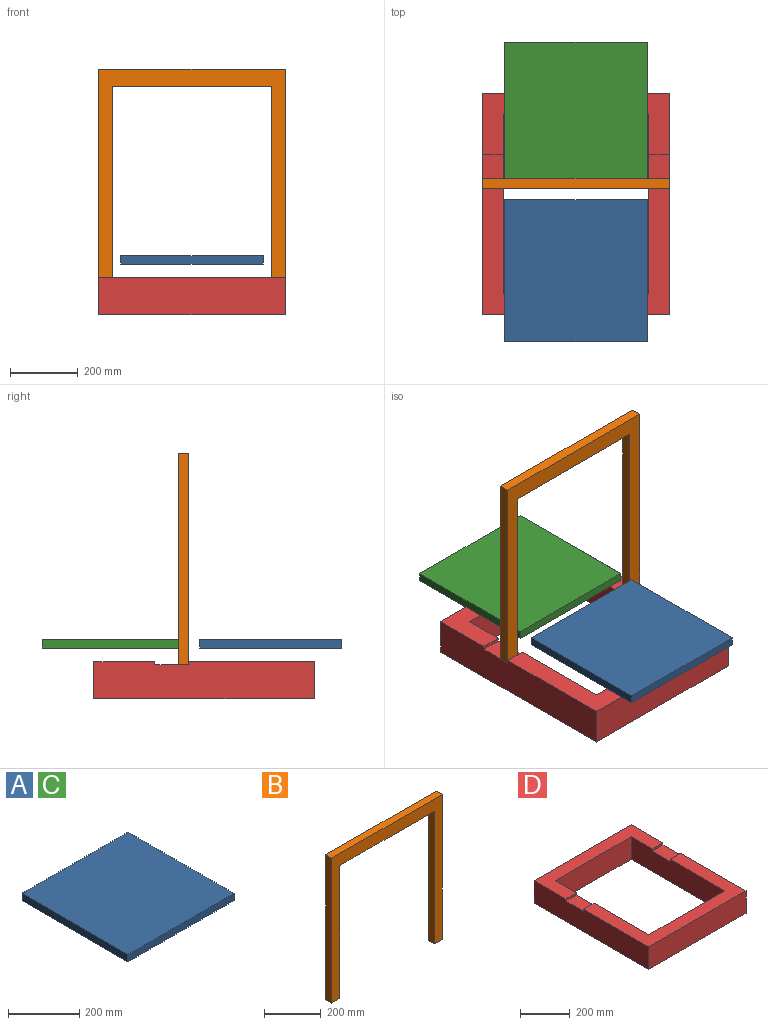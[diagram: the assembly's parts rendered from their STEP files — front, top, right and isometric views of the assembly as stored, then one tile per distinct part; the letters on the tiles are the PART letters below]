
ASSEMBLY  parts=4 mates=5
PART A: 6 faces, bbox 420x420x25 mm
  f0: plane 420x25mm, normal (1,0,0), area 10500mm2, adj f1,f3,f4,f5
  f1: plane 420x25mm, normal (0,1,0), area 10500mm2, adj f0,f2,f4,f5
  f2: plane 420x25mm, normal (-1,0,0), area 10500mm2, adj f1,f3,f4,f5
  f3: plane 420x25mm, normal (0,-1,0), area 10500mm2, adj f0,f2,f4,f5
  f4: plane 420x420mm, normal (0,0,1), area 176400mm2, adj f0,f1,f2,f3
  f5: plane 420x420mm, normal (0,0,-1), area 176400mm2, adj f0,f1,f2,f3
PART B: 10 faces, bbox 550x30x625 mm
  f0: plane 573x30mm, normal (1,0,0), area 17190mm2, adj f1,f7,f8,f9
  f1: plane 470x30mm, normal (0,0,-1), area 14100mm2, adj f0,f2,f8,f9
  f2: plane 573x30mm, normal (-1,0,0), area 17190mm2, adj f1,f3,f8,f9
  f3: plane 40x30mm, normal (0,0,-1), area 1200mm2, adj f2,f4,f8,f9
  f4: plane 625x30mm, normal (1,0,0), area 18750mm2, adj f3,f5,f8,f9
  f5: plane 550x30mm, normal (0,0,1), area 16500mm2, adj f4,f6,f8,f9
  f6: plane 625x30mm, normal (-1,0,0), area 18750mm2, adj f5,f7,f8,f9
  f7: plane 40x30mm, normal (0,0,-1), area 1200mm2, adj f0,f6,f8,f9
  f8: plane 625x550mm, normal (0,-1,0), area 74440mm2, adj f0,f1,f2,f3,f4,f5,f6,f7
  f9: plane 625x550mm, normal (0,1,0), area 74440mm2, adj f0,f1,f2,f3,f4,f5,f6,f7
PART C: same geometry as A
PART D: 17 faces, bbox 550x650x110 mm
  f0: plane 530x110mm, normal (1,0,0), area 57300mm2, adj f3,f7,f8,f9,f10,f11,f12,f13
  f1: plane 530x110mm, normal (-1,0,0), area 57300mm2, adj f3,f7,f8,f9,f10,f14,f15,f16
  f2: plane 650x110mm, normal (-1,0,0), area 70500mm2, adj f3,f4,f6,f9,f10,f11,f12,f13
  f3: plane 550x180mm, normal (0,0,1), area 47400mm2, adj f0,f1,f2,f5,f6,f8,f13,f14
  f4: plane 550x110mm, normal (0,-1,0), area 60500mm2, adj f2,f5,f9,f10
  f5: plane 650x110mm, normal (1,0,0), area 70500mm2, adj f3,f4,f6,f9,f10,f14,f15,f16
  f6: plane 550x110mm, normal (0,1,0), area 60500mm2, adj f2,f3,f5,f10
  f7: plane 430x110mm, normal (0,1,0), area 47300mm2, adj f0,f1,f9,f10
  f8: plane 430x110mm, normal (0,-1,0), area 47300mm2, adj f0,f1,f3,f10
  f9: plane 550x370mm, normal (0,0,1), area 70200mm2, adj f0,f1,f2,f4,f5,f7,f12,f15
  f10: plane 650x550mm, normal (0,0,-1), area 129600mm2, adj f0,f1,f2,f4,f5,f6,f7,f8
  f11: plane 100x60mm, normal (0,0,1), area 6000mm2, adj f0,f2,f12,f13
  f12: plane 60x10mm, normal (0,1,0), area 600mm2, adj f0,f2,f9,f11
  f13: plane 60x10mm, normal (0,-1,0), area 600mm2, adj f0,f2,f3,f11
  f14: plane 60x10mm, normal (0,-1,0), area 600mm2, adj f1,f3,f5,f16
  f15: plane 60x10mm, normal (0,1,0), area 600mm2, adj f1,f5,f9,f16
  f16: plane 100x60mm, normal (0,0,1), area 6000mm2, adj f1,f5,f14,f15
PLACE A rot(axis=(0,0,1),0deg) t=(275,128.03,150)mm
PLACE B t=(0,400,100)mm
PLACE C t=(275,592.66,150)mm
PLACE D at identity
MATE planar B.f6 <-> D.f2  axis (-1,0,0) through (0,385,412.5)mm
MATE planar B.f8 <-> D.f12  axis (0,-1,0) through (275,370,506.56)mm
MATE parallel D.f9 <-> A.f5  axis (0,0,1) through (275,128.03,110)mm
MATE parallel D.f3 <-> C.f5  axis (0,0,1) through (275,592.66,110)mm
MATE planar D.f11 <-> B.f7  axis (0,0,1) through (30,420,100)mm
